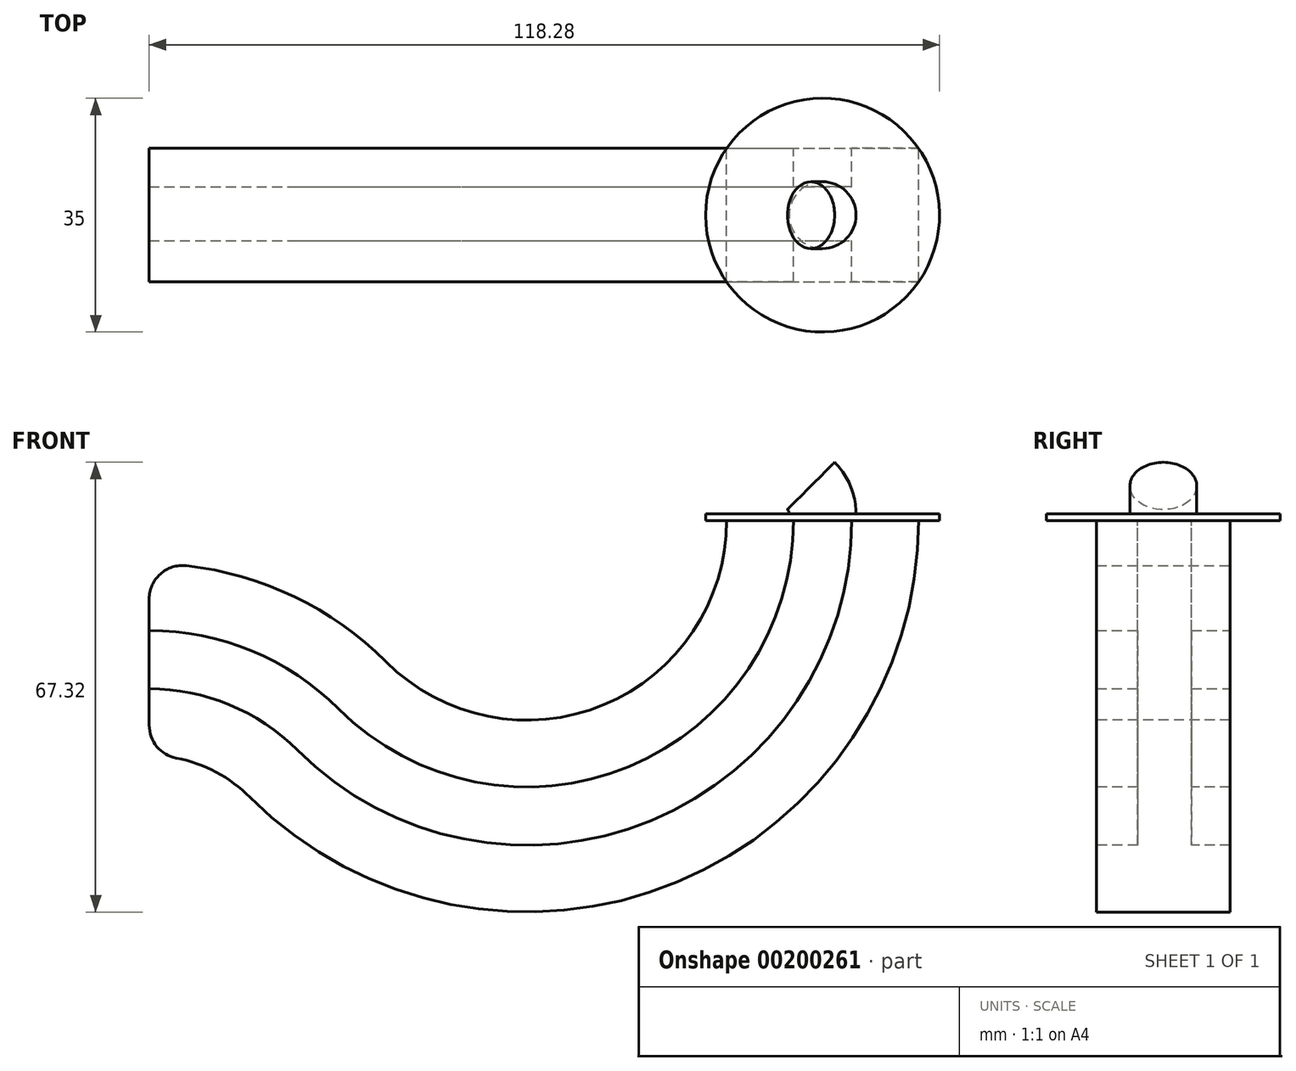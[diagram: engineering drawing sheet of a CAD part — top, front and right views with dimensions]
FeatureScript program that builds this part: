
annotation { "Feature Type Name" : "Feature", "Feature Type Description" : "" }
export const myFeature = defineFeature(function(context is Context, id is Id, definition is map)
    precondition{}
    {
        {
            var Q0;
            Q0=qCreatedBy(makeId("Top.planeOp"),FACE);
            var sketch = newSketch(context, id + "F0", { "sketchPlane" : qUnion([Q0])});
            skCircle(sketch, "E0", {"center": v(17.26, 39.95) * mm, "radius": 5 * mm});
            skLineSegment(sketch, "E1", {"start": v(11.34, 46.2) * mm, "end": v(11.34, 31.4) * mm});
            skSolve(sketch);
        }
        {
            var Q0;
            Q0=makeQuery(id+"F0.imprint","IMPRINT",FACE,{"disambiguationData":[TD([[makeQuery(id+"F0.imprint","IMPRINT",EDGE,{"derivedFrom":sQuery(id+"F0.wireOp",EDGE,"E0")}),1.0]])]});
            var Q1;
            Q1=sQuery(id+"F0.wireOp",EDGE,"E1");
            revolve(context, id + "F1", {"entities" : qUnion([Q0]), "axis" : qUnion([Q1]), "revolveType" : RevolveType.TWO_DIRECTIONS, "angle" : 45 * degree, "angleBack" : 360 * degree});
        }
        {
            var Q0;
            Q0=makeQuery(id+"F1.opRevolve","CAP_FACE",FACE,{"disambiguationData":[OSD([sQuery(id+"F0.wireOp",EDGE,"E0")])],"isStart":true});
            var sketch = newSketch(context, id + "F2", { "sketchPlane" : qUnion([Q0])});
            skCircle(sketch, "E2", {"center": v(17.26, -39.95) * mm, "radius": 17.5 * mm});
            skSolve(sketch);
        }
        {
            var Q0;
            Q0=makeQuery(id+"F2.imprint","IMPRINT",FACE,{"disambiguationData":[TD([[makeQuery(id+"F2.imprint","IMPRINT",EDGE,{"derivedFrom":sQuery(id+"F2.wireOp",EDGE,"E2")}),1.0]])]});
            var Q1;
            Q1=makeQuery(id+"F2.imprint","IMPRINT",FACE,{"disambiguationData":[TD([[makeQuery(id+"F2.imprint","IMPRINT",EDGE,{"derivedFrom":makeQuery(id+"F1.opRevolve","CAP_EDGE",EDGE,{"disambiguationData":[OSD([sQuery(id+"F0.wireOp",EDGE,"E0")])],"isStart":true})}),-1.0]])]});
            extrude(context, id + "F3", {"entities" : qUnion([Q0, Q1]), "operationType" : NewBodyOperationType.ADD, "depth" : 1 * mm});
        }
        {
            var Q0;
            Q0=makeQuery(id+"F3.opExtrude","CAP_FACE",FACE,{"disambiguationData":[OSD([sQuery(id+"F2.wireOp",EDGE,"E2")])],"isStart":false});
            var sketch = newSketch(context, id + "F4", { "sketchPlane" : qUnion([Q0])});
            skLineSegment(sketch, "E3", {"start": v(2.9, -29.95) * mm, "end": v(2.9, -49.95) * mm});
            skLineSegment(sketch, "E4", {"start": v(2.9, -49.95) * mm, "end": v(12.9, -49.95) * mm});
            skLineSegment(sketch, "E5", {"start": v(12.9, -29.95) * mm, "end": v(2.9, -29.95) * mm});
            skPoint(sketch, "E6.middle", {"position": v(17.26, -39.95) * mm});
            skLineSegment(sketch, "E7.bottom", {"start": v(31.62, -29.95) * mm, "end": v(21.62, -29.95) * mm});
            skLineSegment(sketch, "E7.top", {"start": v(31.62, -49.95) * mm, "end": v(21.62, -49.95) * mm});
            skPoint(sketch, "E8", {"position": v(12.9, -36.12) * mm});
            skPoint(sketch, "E9", {"position": v(21.62, -36.12) * mm});
            skPoint(sketch, "E10", {"position": v(12.9, -44.18) * mm});
            skPoint(sketch, "E11", {"position": v(21.62, -44.18) * mm});
            skLineSegment(sketch, "E12", {"start": v(12.9, -44.18) * mm, "end": v(12.9, -49.95) * mm});
            skLineSegment(sketch, "E13", {"start": v(21.62, -29.95) * mm, "end": v(21.62, -36.12) * mm});
            skLineSegment(sketch, "E14", {"start": v(21.62, -44.18) * mm, "end": v(21.62, -49.95) * mm});
            skLineSegment(sketch, "E15", {"start": v(31.62, -29.95) * mm, "end": v(31.62, -49.95) * mm});
            skLineSegment(sketch, "E16", {"start": v(-26.97, -25.42) * mm, "end": v(-26.97, -55.55) * mm});
            skLineSegment(sketch, "E17", {"start": v(12.9, -29.95) * mm, "end": v(12.9, -36.12) * mm});
            skLineSegment(sketch, "E18", {"start": v(12.9, -36.12) * mm, "end": v(21.62, -36.12) * mm});
            skLineSegment(sketch, "E19", {"start": v(21.62, -44.18) * mm, "end": v(12.9, -44.18) * mm});
            skSolve(sketch);
        }
        {
            var Q0;
            Q0=makeQuery(id+"F4.imprint","IMPRINT",FACE,{"disambiguationData":[TD([[makeQuery(id+"F4.imprint","IMPRINT",EDGE,{"derivedFrom":sQuery(id+"F4.wireOp",EDGE,"E3")}),1.0]])]});
            var Q1;
            Q1=makeQuery(id+"F4.imprint","IMPRINT",FACE,{"disambiguationData":[TD([[makeQuery(id+"F4.imprint","IMPRINT",EDGE,{"derivedFrom":sQuery(id+"F4.wireOp",EDGE,"E7.bottom")}),1.0]])]});
            var Q2;
            Q2=sQuery(id+"F4.wireOp",EDGE,"E16");
            revolve(context, id + "F5", {"operationType" : NewBodyOperationType.ADD, "entities" : qUnion([Q0, Q1]), "axis" : qUnion([Q2]), "revolveType" : RevolveType.ONE_DIRECTION, "angle" : 135 * degree});
        }
        {
            var Q0;
            Q0=makeQuery(id+"F5.opRevolve","CAP_FACE",FACE,{"disambiguationData":[OSD([sQuery(id+"F4.wireOp",EDGE,"E3"),sQuery(id+"F4.wireOp",EDGE,"E4"),sQuery(id+"F4.wireOp",EDGE,"E5"),sQuery(id+"F4.wireOp",EDGE,"E7.bottom"),sQuery(id+"F4.wireOp",EDGE,"E7.top"),sQuery(id+"F4.wireOp",EDGE,"8fVzqQoe-QOPs-ZCh5-ai9C-A4RtrGaLOi3c"),sQuery(id+"F4.wireOp",EDGE,"dCLopN7q-dHg6-Dtuh-PpNe-Q6AOM9fsKLdI"),sQuery(id+"F4.wireOp",EDGE,"nyfnzoNK-QgQO-hLSM-gTAi-vVS44sqsABuP"),sQuery(id+"F4.wireOp",EDGE,"E12"),sQuery(id+"F4.wireOp",EDGE,"E13"),sQuery(id+"F4.wireOp",EDGE,"E14"),sQuery(id+"F4.wireOp",EDGE,"E15")])],"isStart":false});
            var sketch = newSketch(context, id + "F6", { "sketchPlane" : qUnion([Q0])});
            skLineSegment(sketch, "E20", {"start": v(-20.63, -99.75) * mm, "end": v(-64.1, -99.75) * mm});
            skSolve(sketch);
        }
        {
            var Q0;
            Q0=makeQuery(id+"F6.imprint","IMPRINT",FACE,{"disambiguationData":[TD([[makeQuery(id+"F6.imprint","IMPRINT",EDGE,{"derivedFrom":makeQuery(id+"F5.opRevolve","CAP_EDGE",EDGE,{"disambiguationData":[OSD([sQuery(id+"F4.wireOp",EDGE,"E3")])],"isStart":false})}),1.0]])]});
            var Q1;
            Q1=sQuery(id+"F6.wireOp",EDGE,"E20");
            revolve(context, id + "F7", {"operationType" : NewBodyOperationType.ADD, "entities" : qUnion([Q0]), "axis" : qUnion([Q1]), "revolveType" : RevolveType.ONE_DIRECTION, "oppositeDirection" : true, "angle" : 45 * degree});
        }
        {
            var Q0;
            Q0=makeQuery(id+"F7.opRevolve","CAP_EDGE",EDGE,{"disambiguationData":[OSD([sQuery(id+"F4.wireOp",EDGE,"E15")])],"isStart":false});
            fillet(context, id + "F8", {"entities" : qUnion([Q0]), "radius" : 5 * mm, "tangentPropagation" : true, "allowEdgeOverflow" : false});
        }
        {
            var Q0;
            Q0=makeQuery(id+"F7.opRevolve","CAP_EDGE",EDGE,{"disambiguationData":[OSD([sQuery(id+"F4.wireOp",EDGE,"E3")])],"isStart":false});
            fillet(context, id + "F9", {"entities" : qUnion([Q0]), "radius" : 5 * mm, "tangentPropagation" : true, "allowEdgeOverflow" : false});
        }
    });
